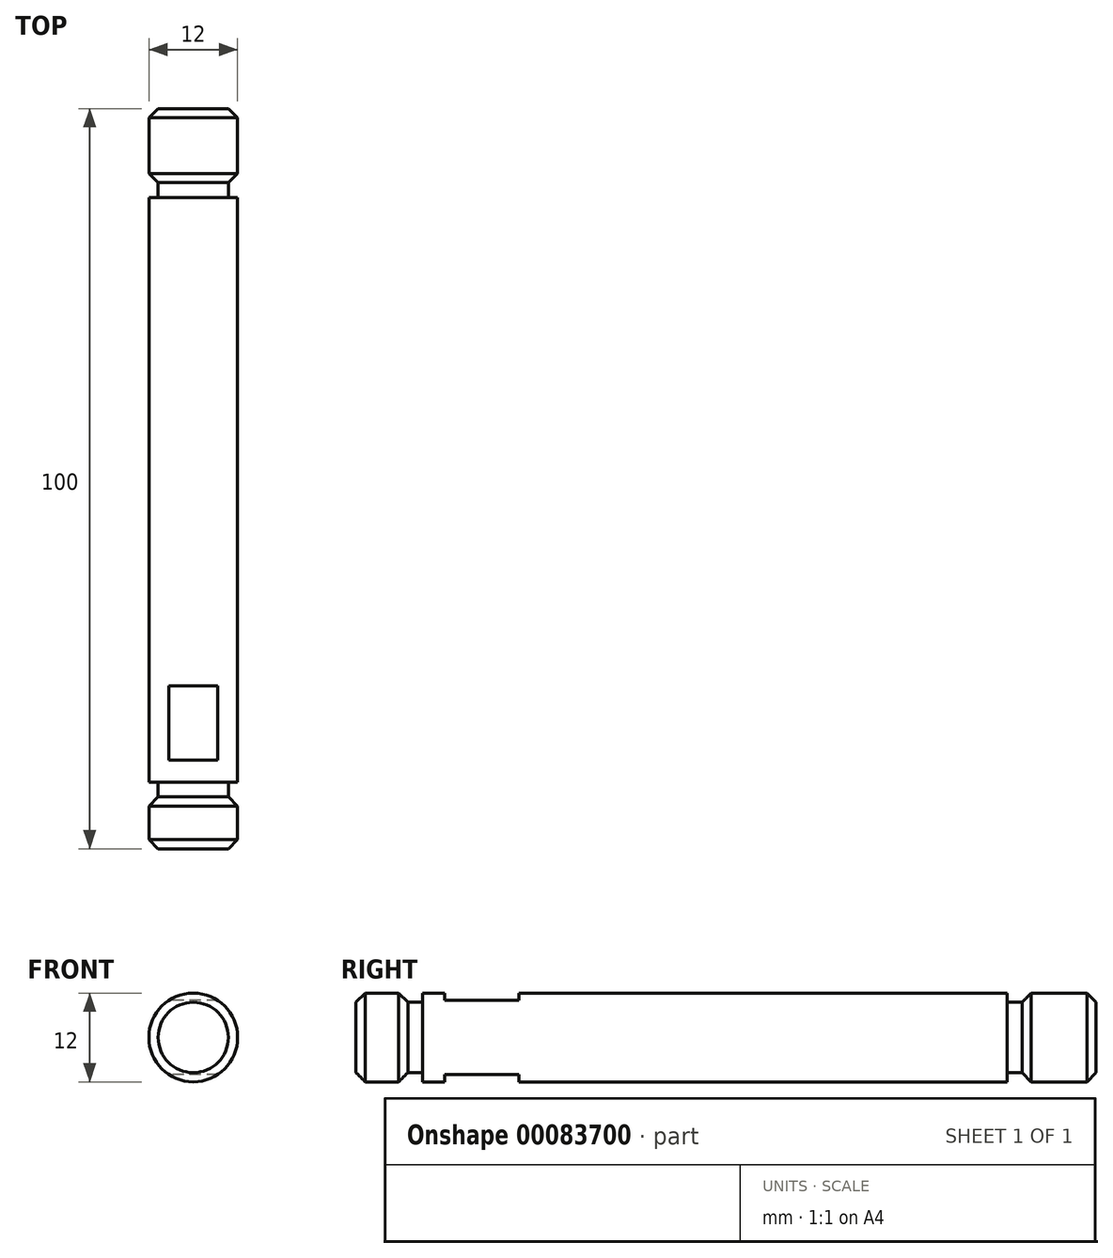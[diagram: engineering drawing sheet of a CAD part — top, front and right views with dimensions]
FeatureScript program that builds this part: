
annotation { "Feature Type Name" : "Feature", "Feature Type Description" : "" }
export const myFeature = defineFeature(function(context is Context, id is Id, definition is map)
    precondition{}
    {
        {
            var Q0;
            Q0=qCreatedBy(makeId("Front.planeOp"),FACE);
            var sketch = newSketch(context, id + "F0", { "sketchPlane" : qUnion([Q0])});
            skCircle(sketch, "E0", {"center": v(0, 0) * mm, "radius": 6 * mm});
            skSolve(sketch);
        }
        {
            var Q0;
            Q0=qSketchRegion(id+"F0",true);
            extrude(context, id + "F1", {"entities" : qUnion([Q0]), "oppositeDirection" : true, "depth" : 7 * mm});
        }
        {
            var Q0;
            Q0=makeQuery(id+"F1.opExtrude","CAP_FACE",FACE,{"disambiguationData":[OSD([sQuery(id+"F0.wireOp",EDGE,"E0")])],"isStart":false});
            var sketch = newSketch(context, id + "F2", { "sketchPlane" : qUnion([Q0])});
            skCircle(sketch, "E1", {"center": v(0, 0) * mm, "radius": 4.75 * mm});
            skSolve(sketch);
        }
        {
            var Q0;
            Q0=makeQuery(id+"F2.imprint","IMPRINT",FACE,{"disambiguationData":[TD([[makeQuery(id+"F2.imprint","IMPRINT",EDGE,{"derivedFrom":sQuery(id+"F2.wireOp",EDGE,"E1")}),1.0]])]});
            extrude(context, id + "F3", {"entities" : qUnion([Q0]), "operationType" : NewBodyOperationType.ADD, "depth" : 2 * mm});
        }
        {
            var Q0;
            Q0=makeQuery(id+"F3.opExtrude","CAP_FACE",FACE,{"disambiguationData":[OSD([sQuery(id+"F2.wireOp",EDGE,"E1")])],"isStart":false});
            var sketch = newSketch(context, id + "F4", { "sketchPlane" : qUnion([Q0])});
            skCircle(sketch, "E2", {"center": v(0, 0) * mm, "radius": 6 * mm});
            skSolve(sketch);
        }
        {
            var Q0;
            Q0=qSketchRegion(id+"F4",true);
            extrude(context, id + "F5", {"entities" : qUnion([Q0]), "operationType" : NewBodyOperationType.ADD, "depth" : (91 - 12) * mm});
        }
        {
            var Q0;
            Q0=makeQuery(id+"F5.opExtrude","CAP_FACE",FACE,{"disambiguationData":[OSD([sQuery(id+"F4.wireOp",EDGE,"E2")])],"isStart":false});
            var sketch = newSketch(context, id + "F6", { "sketchPlane" : qUnion([Q0])});
            skCircle(sketch, "E3", {"center": v(0, 0) * mm, "radius": 4.75 * mm});
            skSolve(sketch);
        }
        {
            var Q0;
            Q0=qSketchRegion(id+"F6",true);
            extrude(context, id + "F7", {"entities" : qUnion([Q0]), "operationType" : NewBodyOperationType.ADD, "depth" : 2 * mm});
        }
        {
            var Q0;
            Q0=makeQuery(id+"F7.opExtrude","CAP_FACE",FACE,{"disambiguationData":[OSD([sQuery(id+"F6.wireOp",EDGE,"E3")])],"isStart":false});
            var sketch = newSketch(context, id + "F8", { "sketchPlane" : qUnion([Q0])});
            skCircle(sketch, "E4", {"center": v(0, 0) * mm, "radius": 6 * mm});
            skSolve(sketch);
        }
        {
            var Q0;
            Q0=qSketchRegion(id+"F8",true);
            extrude(context, id + "F9", {"entities" : qUnion([Q0]), "operationType" : NewBodyOperationType.ADD, "depth" : 10 * mm});
        }
        {
            var Q0;
            Q0=makeQuery(id+"F1.opExtrude","SWEPT_FACE",FACE,{"disambiguationData":[OSD([sQuery(id+"F0.wireOp",EDGE,"E0")])]});
            var Q1;
            Q1=makeQuery(id+"F9.opExtrude","SWEPT_FACE",FACE,{"disambiguationData":[OSD([sQuery(id+"F8.wireOp",EDGE,"E4")])]});
            chamfer(context, id + "F10", {"entities" : qUnion([Q0, Q1]), "width" : 1.25 * mm, "tangentPropagation" : true});
        }
        {
            var Q0;
            Q0=qCreatedBy(makeId("Top.planeOp"),FACE);
            cPlane(context, id + "F11", {"entities" : qUnion([Q0]), "cplaneType" : CPlaneType.OFFSET, "offset" : 6 * mm, "width" : 150 * mm, "height" : 150 * mm});
        }
        {
            var Q0;
            Q0=qCreatedBy(id+"F11.planeOp",FACE);
            var sketch = newSketch(context, id + "F12", { "sketchPlane" : qUnion([Q0])});
            skLineSegment(sketch, "E5.rect.bottom", {"start": v(6.5, 22) * mm, "end": v(-6.5, 22) * mm});
            skLineSegment(sketch, "E5.rect.top", {"start": v(6.5, 12) * mm, "end": v(-6.5, 12) * mm});
            skLineSegment(sketch, "E5.rect.left", {"start": v(6.5, 22) * mm, "end": v(6.5, 12) * mm});
            skLineSegment(sketch, "E5.rect.right", {"start": v(-6.5, 22) * mm, "end": v(-6.5, 12) * mm});
            skPoint(sketch, "E5.rect.middle", {"position": v(0, 17) * mm});
            skSolve(sketch);
        }
        {
            var Q0;
            Q0=qSketchRegion(id+"F12",true);
            extrude(context, id + "F13", {"entities" : qUnion([Q0]), "operationType" : NewBodyOperationType.REMOVE, "oppositeDirection" : true, "depth" : 1 * mm});
        }
        {
            var Q0;
            Q0=makeQuery(id+"F13.boolean.opBoolean","COPY",FACE,{"derivedFrom":makeQuery(id+"F13.opExtrude","CAP_FACE",FACE,{"disambiguationData":[OSD([sQuery(id+"F12.wireOp",EDGE,"E5.rect.bottom"),sQuery(id+"F12.wireOp",EDGE,"E5.rect.top"),sQuery(id+"F12.wireOp",EDGE,"E5.rect.left"),sQuery(id+"F12.wireOp",EDGE,"E5.rect.right")])],"isStart":false})});
            var Q1;
            Q1=makeQuery(id+"F13.boolean.opBoolean","COPY",FACE,{"derivedFrom":makeQuery(id+"F13.opExtrude","SWEPT_FACE",FACE,{"disambiguationData":[OSD([sQuery(id+"F12.wireOp",EDGE,"E5.rect.bottom")])]})});
            var Q2;
            Q2=makeQuery(id+"F13.boolean.opBoolean","COPY",FACE,{"derivedFrom":makeQuery(id+"F13.opExtrude","SWEPT_FACE",FACE,{"disambiguationData":[OSD([sQuery(id+"F12.wireOp",EDGE,"E5.rect.top")])]})});
            var Q3;
            Q3=qCreatedBy(makeId("Top.planeOp"),FACE);
            mirror(context, id + "F14", {"operationType" : NewBodyOperationType.INTERSECT, "faces" : qUnion([Q0, Q1, Q2]), "mirrorPlane" : qUnion([Q3]), "patternType" : MirrorType.FACE});
        }
    });
